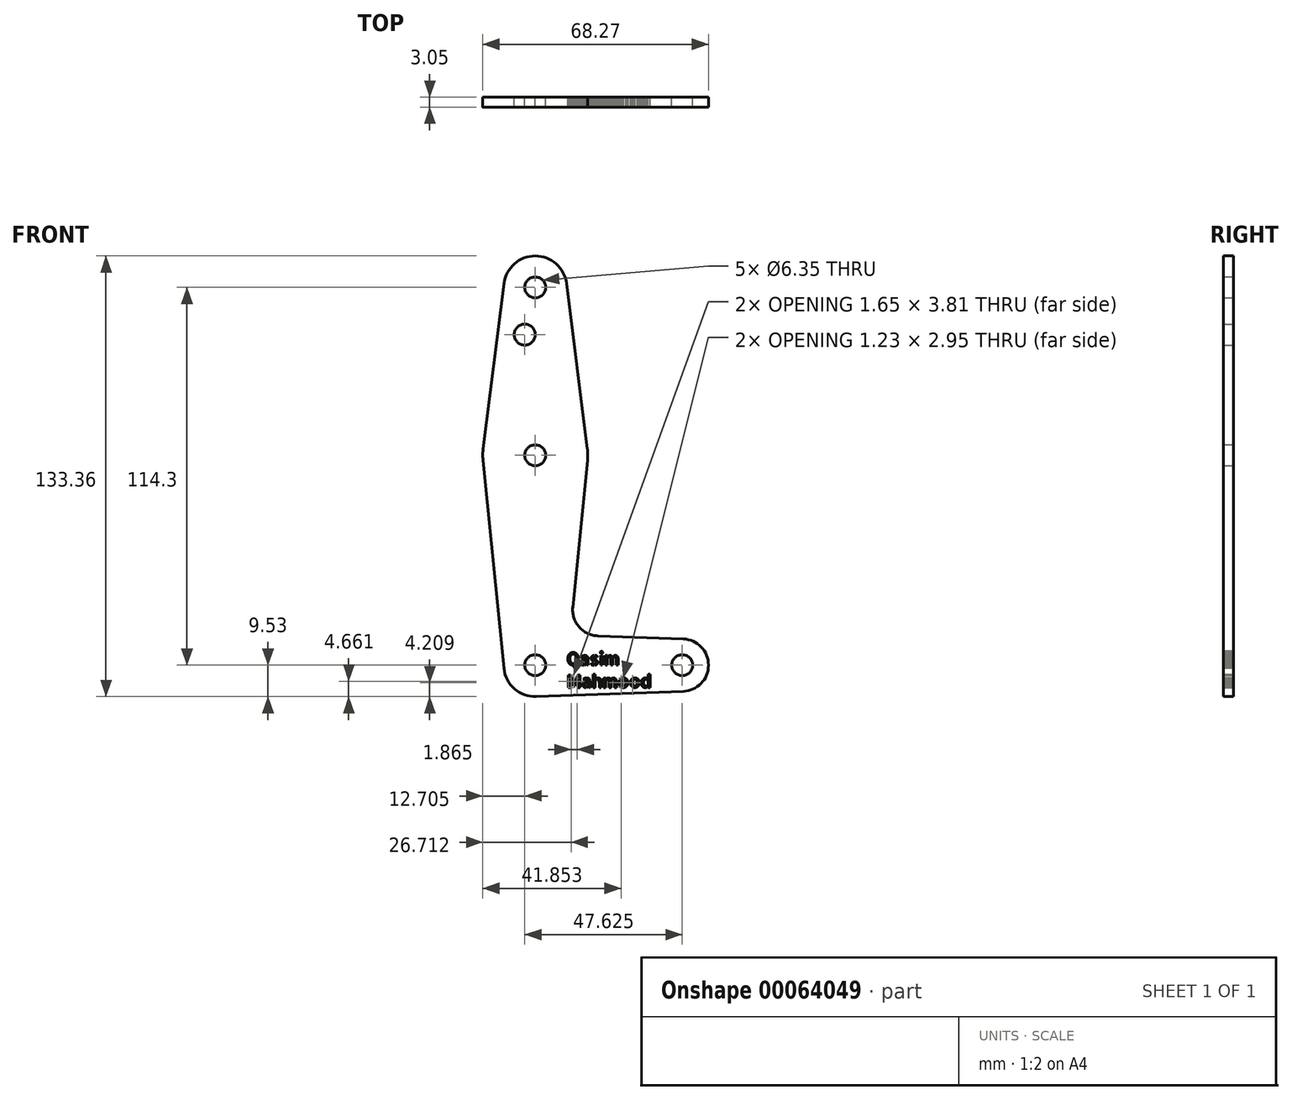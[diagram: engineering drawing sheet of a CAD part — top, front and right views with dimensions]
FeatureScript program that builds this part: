
annotation { "Feature Type Name" : "Feature", "Feature Type Description" : "" }
export const myFeature = defineFeature(function(context is Context, id is Id, definition is map)
    precondition{}
    {
        {
            var Q0;
            Q0=qCreatedBy(makeId("Front.planeOp"),FACE);
            var sketch = newSketch(context, id + "F0", { "sketchPlane" : qUnion([Q0])});
            skLineSegment(sketch, "E0", {"start": v(44.45, 0) * mm, "end": v(0, 0) * mm, "construction": true});
            skLineSegment(sketch, "E1", {"start": v(0, 0) * mm, "end": v(0, 114.3) * mm, "construction": true});
            skCircle(sketch, "E2", {"center": v(0, 0) * mm, "radius": 9.53 * mm});
            skCircle(sketch, "E3", {"center": v(0, 63.5) * mm, "radius": 15.88 * mm});
            skCircle(sketch, "E4", {"center": v(0, 114.3) * mm, "radius": 9.53 * mm});
            skCircle(sketch, "E5", {"center": v(44.45, 0) * mm, "radius": 7.94 * mm});
            skLineSegment(sketch, "E6", {"start": v(-9.45, 115.5) * mm, "end": v(-15.75, 65.48) * mm});
            skLineSegment(sketch, "E7", {"start": v(15.75, 65.48) * mm, "end": v(9.45, 115.5) * mm});
            skLineSegment(sketch, "E8", {"start": v(-15.8, 61.91) * mm, "end": v(-9.48, -0.95) * mm});
            skLineSegment(sketch, "E9", {"start": v(11.34, 17.6) * mm, "end": v(15.8, 61.91) * mm});
            skLineSegment(sketch, "E10", {"start": v(18.97, 8.85) * mm, "end": v(44.73, 7.93) * mm});
            skLineSegment(sketch, "E11", {"start": v(44.73, -7.93) * mm, "end": v(0.34, -9.52) * mm});
            skCircle(sketch, "E12", {"center": v(0, 114.3) * mm, "radius": 3.18 * mm});
            skCircle(sketch, "E13", {"center": v(0, 63.5) * mm, "radius": 3.18 * mm});
            skCircle(sketch, "E14", {"center": v(0, 0) * mm, "radius": 3.18 * mm});
            skCircle(sketch, "E15", {"center": v(44.45, 0) * mm, "radius": 3.18 * mm});
            skCircle(sketch, "E16", {"center": v(-3.18, 100.03) * mm, "radius": 3.18 * mm});
            skArc(sketch, "E17.filletArc", {"start": v(11.34, 17.6) * mm, "mid": v(13.26, 11.57) * mm, "end": v(18.97, 8.85) * mm});
            skText(sketch, "E18", { "text": "Qasim\nMahmood", "fontName": "AllertaStencil-Regular.ttf"});
            const initialGuessF0  = {"E18": [0.00953, 0, 1, 0, 0.00381]};
            skSetInitialGuess(sketch, initialGuessF0);
            skSolve(sketch);
        }
        {
            var Q0;
            Q0 = qSketchRegion(id + "F0", true);
            extrude(context, id + "F1", {"entities" : qUnion([Q0]), "depth" : 3.05 * mm});
        }
    });
